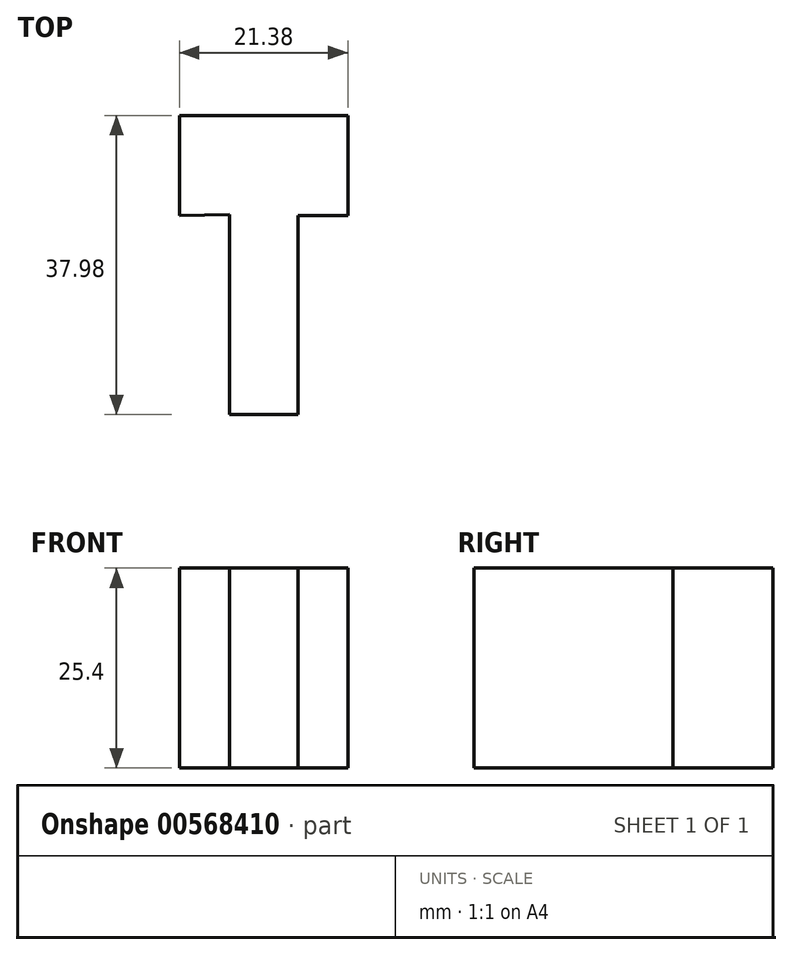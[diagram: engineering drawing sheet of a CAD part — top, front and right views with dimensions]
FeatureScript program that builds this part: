
annotation { "Feature Type Name" : "Feature", "Feature Type Description" : "" }
export const myFeature = defineFeature(function(context is Context, id is Id, definition is map)
    precondition{}
    {
        {
            var Q0;
            Q0=qCreatedBy(makeId("Top.planeOp"),FACE);
            var sketch = newSketch(context, id + "F0", { "sketchPlane" : qUnion([Q0])});
            skLineSegment(sketch, "E0", {"start": v(-34.09, 25.4) * mm, "end": v(-34.09, 0) * mm});
            skLineSegment(sketch, "E1", {"start": v(-34.09, 0) * mm, "end": v(-21.39, 0) * mm});
            skLineSegment(sketch, "E2", {"start": v(-25.4, -0.12) * mm, "end": v(-25.4, 25.28) * mm});
            skLineSegment(sketch, "E3", {"start": v(-25.4, 25.28) * mm, "end": v(-19.05, 25.28) * mm});
            skLineSegment(sketch, "E4", {"start": v(-19.05, 25.28) * mm, "end": v(-19.05, 37.98) * mm});
            skLineSegment(sketch, "E5", {"start": v(-15.03, 37.98) * mm, "end": v(-40.43, 37.98) * mm});
            skLineSegment(sketch, "E6", {"start": v(-40.43, 37.98) * mm, "end": v(-40.43, 25.28) * mm});
            skLineSegment(sketch, "E7", {"start": v(-40.43, 25.28) * mm, "end": v(-34.09, 25.4) * mm});
            skSolve(sketch);
        }
        {
            var Q0;
            Q0 = qSketchRegion(id + "F0", true);
            extrude(context, id + "F1", {"entities" : qUnion([Q0]), "depth" : 25.4 * mm, "offsetDistance" : 25.4 * mm});
        }
    });
